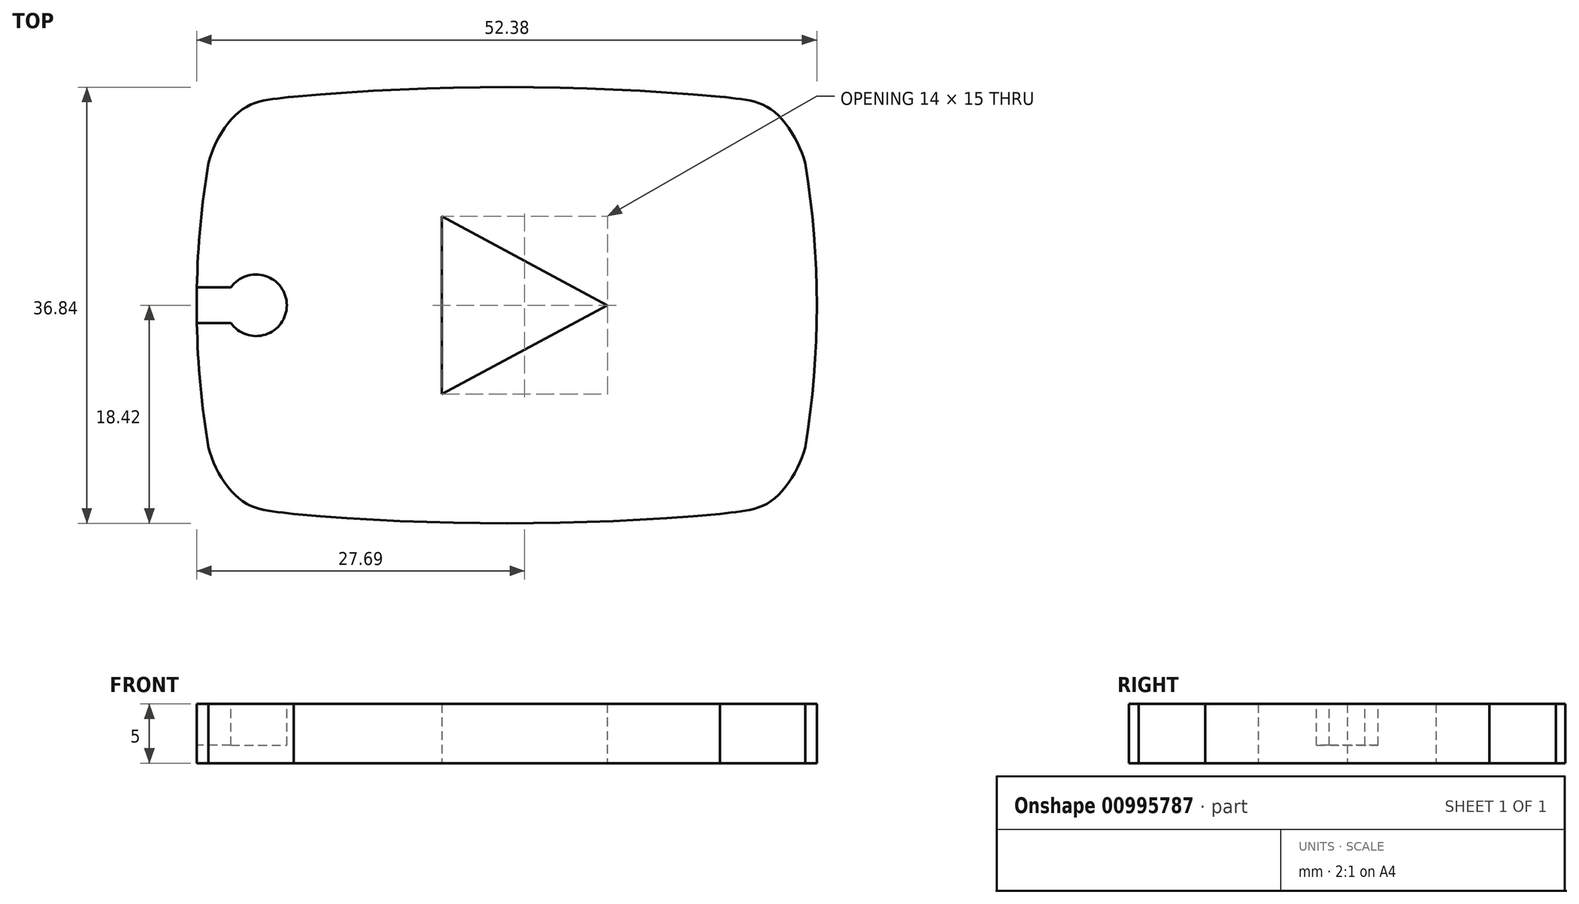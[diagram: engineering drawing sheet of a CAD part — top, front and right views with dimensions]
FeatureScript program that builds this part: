
annotation { "Feature Type Name" : "Feature", "Feature Type Description" : "" }
export const myFeature = defineFeature(function(context is Context, id is Id, definition is map)
    precondition{}
    {
        {
            var Q0;
            Q0=qCreatedBy(makeId("Top.planeOp"),FACE);
            var sketch = newSketch(context, id + "F0", { "sketchPlane" : qUnion([Q0])});
            skPoint(sketch, "E0.middle", {"position": v(0, 0) * mm});
            skLineSegment(sketch, "E1", {"start": v(0, -18.42) * mm, "end": v(0, 18.42) * mm, "construction": true});
            skLineSegment(sketch, "E2", {"start": v(-30, 0) * mm, "end": v(30, 0) * mm, "construction": true});
            skArc(sketch, "E3", {"start": v(-25.2, 12) * mm, "mid": v(-26.2, 0) * mm, "end": v(-25.2, -12) * mm});
            skArc(sketch, "E4", {"start": v(18, 17.62) * mm, "mid": v(0, 18.42) * mm, "end": v(-18, 17.62) * mm});
            skFitSpline(sketch, "E5", {"points": [v(-25.2, 12) * mm, v(-22.27, 16.57) * mm, v(-18, 17.62) * mm], "startDerivative": vector(2.45, 9.87) * mm, "endDerivative": vector(11.01, 1.4) * mm});
            skFitSpline(sketch, "E6.MirrorCS", {"points": [v(25.2, 12) * mm, v(22.27, 16.57) * mm, v(18, 17.62) * mm], "startDerivative": vector(-2.45, 9.87) * mm, "endDerivative": vector(-11.01, 1.4) * mm});
            skArc(sketch, "E7.MirrorCS", {"start": v(25.2, 12) * mm, "mid": v(26.2, 0) * mm, "end": v(25.2, -12) * mm});
            skFitSpline(sketch, "E8.MirrorCS", {"points": [v(25.2, -12) * mm, v(22.27, -16.57) * mm, v(18, -17.62) * mm], "startDerivative": vector(-2.45, -9.87) * mm, "endDerivative": vector(-11.01, -1.4) * mm});
            skArc(sketch, "E9.MirrorCS", {"start": v(18, -17.62) * mm, "mid": v(0, -18.42) * mm, "end": v(-18, -17.62) * mm});
            skFitSpline(sketch, "E10.MirrorCS", {"points": [v(-25.2, -12) * mm, v(-22.27, -16.57) * mm, v(-18, -17.62) * mm], "startDerivative": vector(2.45, -9.87) * mm, "endDerivative": vector(11.01, -1.4) * mm});
            skLineSegment(sketch, "E11", {"start": v(-5.5, 7.5) * mm, "end": v(-5.5, -7.5) * mm});
            skLineSegment(sketch, "E12", {"start": v(-5.5, -7.5) * mm, "end": v(8.5, 0) * mm});
            skLineSegment(sketch, "E13", {"start": v(8.5, 0) * mm, "end": v(-5.5, 7.5) * mm});
            skSolve(sketch);
        }
        {
            var Q0;
            Q0=qSketchRegion(id+"F0",true);
            extrude(context, id + "F1", {"entities" : qUnion([Q0]), "depth" : 5 * mm, "offsetDistance" : 25 * mm});
        }
        {
            var Q0;
            Q0=makeQuery(id+"F1.opExtrude","SWEPT_BODY",BODY,{"disambiguationData":[OSD([sQuery(id+"F0.wireOp",EDGE,"E3"),sQuery(id+"F0.wireOp",EDGE,"E4"),sQuery(id+"F0.wireOp",EDGE,"E5"),sQuery(id+"F0.wireOp",EDGE,"E6.MirrorCS"),sQuery(id+"F0.wireOp",EDGE,"E7.MirrorCS"),sQuery(id+"F0.wireOp",EDGE,"E8.MirrorCS"),sQuery(id+"F0.wireOp",EDGE,"E9.MirrorCS"),sQuery(id+"F0.wireOp",EDGE,"E10.MirrorCS"),sQuery(id+"F0.wireOp",EDGE,"E11"),sQuery(id+"F0.wireOp",EDGE,"E12"),sQuery(id+"F0.wireOp",EDGE,"E13")])]});
            var Q1;
            Q1=qCreatedBy(makeId("Origin.pointOp"),VERTEX);
            var Q2;
            Q2=qCreatedBy(makeId("Origin.pointOp"),VERTEX);
            transform(context, id + "F2", {"entities" : qUnion([Q0]), "transformType" : TransformType.SCALE_UNIFORMLY, "scale" : 1, "scalePoint" : qUnion([Q2]), "makeCopy" : false});
        }
        {
            var Q0;
            Q0=makeQuery(id+"F1.opExtrude","CAP_FACE",FACE,{"disambiguationData":[OSD([sQuery(id+"F0.wireOp",EDGE,"E3"),sQuery(id+"F0.wireOp",EDGE,"E4"),sQuery(id+"F0.wireOp",EDGE,"E5"),sQuery(id+"F0.wireOp",EDGE,"E6.MirrorCS"),sQuery(id+"F0.wireOp",EDGE,"E7.MirrorCS"),sQuery(id+"F0.wireOp",EDGE,"E8.MirrorCS"),sQuery(id+"F0.wireOp",EDGE,"E9.MirrorCS"),sQuery(id+"F0.wireOp",EDGE,"E10.MirrorCS"),sQuery(id+"F0.wireOp",EDGE,"E11"),sQuery(id+"F0.wireOp",EDGE,"E12"),sQuery(id+"F0.wireOp",EDGE,"E13")])],"isStart":false});
            var sketch = newSketch(context, id + "F3", { "sketchPlane" : qUnion([Q0])});
            skCircle(sketch, "E14", {"center": v(-21.18, 0) * mm, "radius": 2.6 * mm});
            skLineSegment(sketch, "E15", {"start": v(-23.3, 1.5) * mm, "end": v(-26.18, 1.5) * mm});
            skLineSegment(sketch, "E16.MirrorCS", {"start": v(-23.3, -1.5) * mm, "end": v(-26.18, -1.5) * mm});
            skSolve(sketch);
        }
        {
            var Q0;
            {var subQ0=sQuery(id+"F3.wireOp",EDGE,"E15");Q0=makeQuery(id+"F3.imprint","IMPRINT",FACE,{"disambiguationData":[TD([[makeQuery(id+"F3.imprint","IMPRINT",EDGE,{"derivedFrom":subQ0}),1.0]])]});}
            var Q1;
            {var subQ0=sQuery(id+"F3.wireOp",EDGE,"E14");var subQ1=makeQuery(id+"F3.imprint","INTERSECT",VERTEX,{"derivedFrom":[subQ0,sQuery(id+"F3.wireOp",EDGE,"E15")]});Q1=makeQuery(id+"F3.imprint","IMPRINT",FACE,{"disambiguationData":[TD([[makeQuery(id+"F3.imprint","IMPRINT",EDGE,{"disambiguationData":[TD([[subQ1,-1.0]])],"derivedFrom":subQ0}),1.0]])]});}
            extrude(context, id + "F4", {"entities" : qUnion([Q0, Q1]), "operationType" : NewBodyOperationType.REMOVE, "oppositeDirection" : true, "depth" : 3.5 * mm, "offsetDistance" : 25 * mm});
        }
    });
